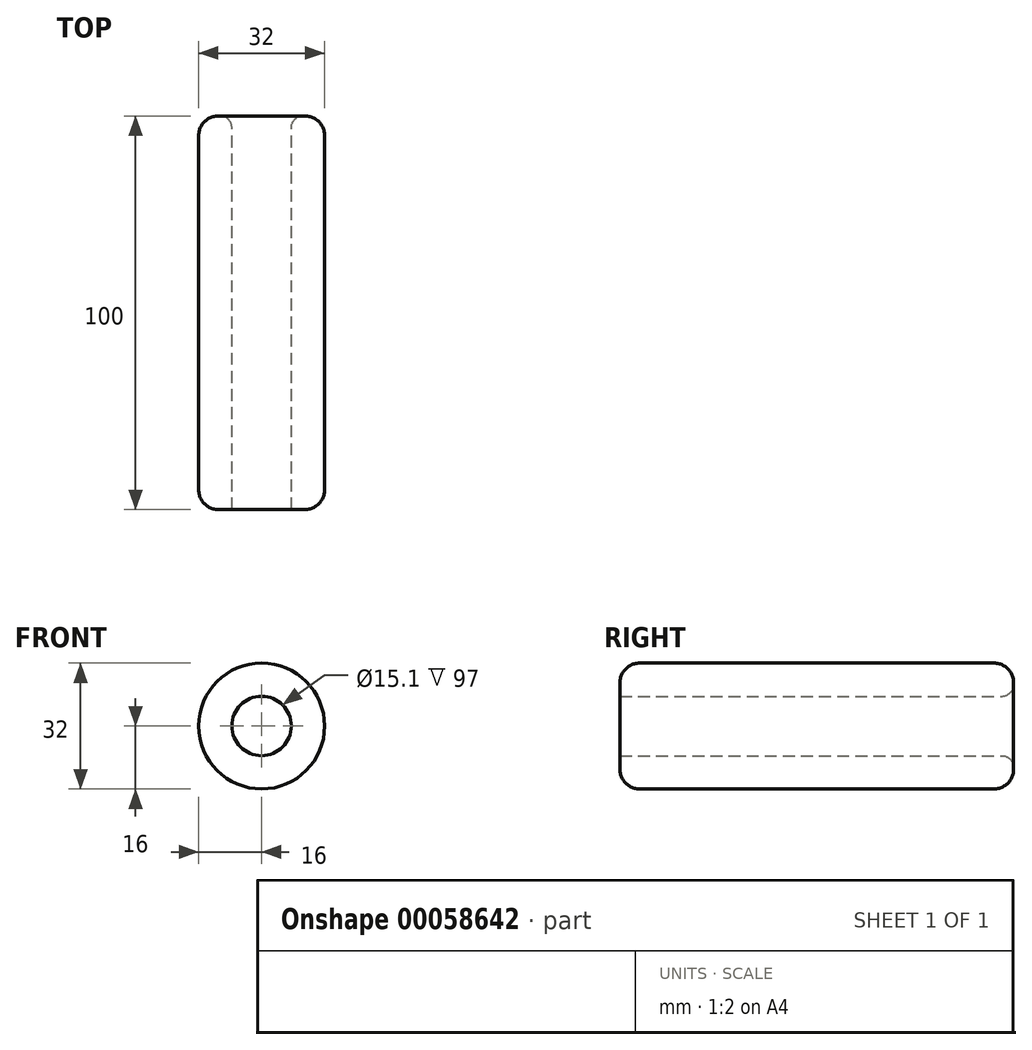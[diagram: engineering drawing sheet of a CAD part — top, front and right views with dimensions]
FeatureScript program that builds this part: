
annotation { "Feature Type Name" : "Feature", "Feature Type Description" : "" }
export const myFeature = defineFeature(function(context is Context, id is Id, definition is map)
    precondition{}
    {
        {
            var Q0;
            Q0=qCreatedBy(makeId("Front.planeOp"),FACE);
            var sketch = newSketch(context, id + "F0", { "sketchPlane" : qUnion([Q0])});
            skCircle(sketch, "E0", {"center": v(0, 0) * mm, "radius": 7.55 * mm});
            skCircle(sketch, "E1", {"center": v(0, 0) * mm, "radius": 16 * mm});
            skSolve(sketch);
        }
        {
            var Q0;
            Q0=qSketchRegion(id+"F0",true);
            extrude(context, id + "F1", {"entities" : qUnion([Q0]), "depth" : 100 * mm});
        }
        {
            var Q0;
            Q0=makeQuery(id+"F1.opExtrude","CAP_EDGE",EDGE,{"disambiguationData":[OSD([sQuery(id+"F0.wireOp",EDGE,"E1")])],"isStart":false});
            var Q1;
            Q1=makeQuery(id+"F1.opExtrude","CAP_EDGE",EDGE,{"disambiguationData":[OSD([sQuery(id+"F0.wireOp",EDGE,"E1")])],"isStart":true});
            fillet(context, id + "F2", {"entities" : qUnion([Q0, Q1]), "radius" : 5 * mm, "tangentPropagation" : true, "allowEdgeOverflow" : false});
        }
        {
            var Q0;
            Q0=makeQuery(id+"F1.opExtrude","CAP_EDGE",EDGE,{"disambiguationData":[OSD([sQuery(id+"F0.wireOp",EDGE,"E0")])],"isStart":true});
            fillet(context, id + "F3", {"entities" : qUnion([Q0]), "radius" : 3 * mm, "tangentPropagation" : true, "allowEdgeOverflow" : false});
        }
    });
